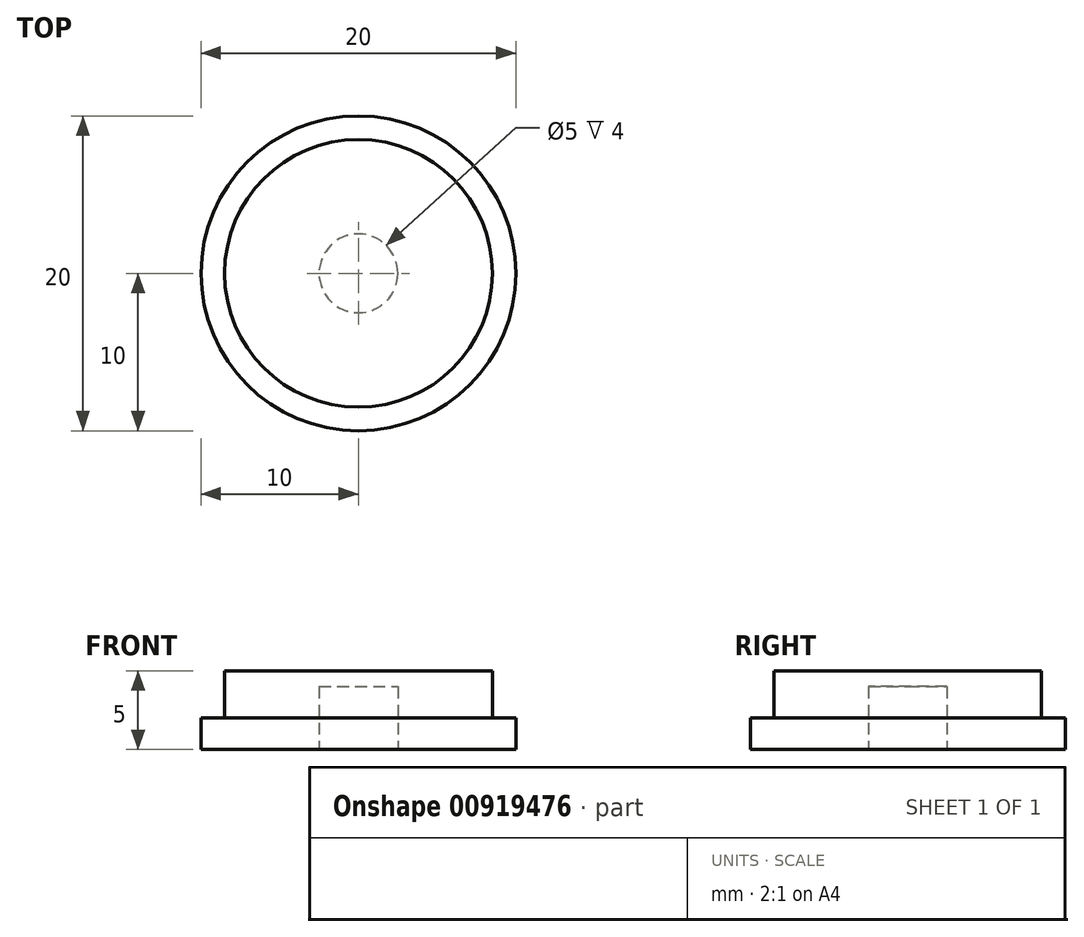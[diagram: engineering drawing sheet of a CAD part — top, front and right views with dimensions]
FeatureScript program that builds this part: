
annotation { "Feature Type Name" : "Feature", "Feature Type Description" : "" }
export const myFeature = defineFeature(function(context is Context, id is Id, definition is map)
    precondition{}
    {
        {
            var Q0;
            Q0=qCreatedBy(makeId("Top.planeOp"),FACE);
            var sketch = newSketch(context, id + "F0", { "sketchPlane" : qUnion([Q0])});
            skCircle(sketch, "E0", {"center": v(0, 0) * mm, "radius": 10 * mm});
            skSolve(sketch);
        }
        {
            var Q0;
            Q0 = qSketchRegion(id + "F0", true);
            extrude(context, id + "F1", {"entities" : qUnion([Q0]), "depth" : 5 * mm, "offsetDistance" : 25 * mm, "symmetric" : true});
        }
        {
            var Q0;
            Q0=makeQuery(id+"F1.opExtrude","CAP_FACE",FACE,{"disambiguationData":[OSD([sQuery(id+"F0.wireOp",EDGE,"E0")])],"isStart":false});
            var sketch = newSketch(context, id + "F2", { "sketchPlane" : qUnion([Q0])});
            skCircle(sketch, "E1", {"center": v(0, 0) * mm, "radius": 10 * mm});
            skCircle(sketch, "E2.0", {"center": v(0, 0) * mm, "radius": 8.5 * mm});
            skSolve(sketch);
        }
        {
            var Q0;
            Q0 = qSketchRegion(id + "F2", true);
            extrude(context, id + "F3", {"entities" : qUnion([Q0]), "operationType" : NewBodyOperationType.REMOVE, "oppositeDirection" : true, "depth" : 3 * mm, "offsetDistance" : 25 * mm});
        }
        {
            var Q0;
            Q0=makeQuery(id+"F1.opExtrude","CAP_FACE",FACE,{"disambiguationData":[OSD([sQuery(id+"F0.wireOp",EDGE,"E0")])],"isStart":true});
            var sketch = newSketch(context, id + "F4", { "sketchPlane" : qUnion([Q0])});
            skCircle(sketch, "E3", {"center": v(0, 0) * mm, "radius": 2.5 * mm});
            skSolve(sketch);
        }
        {
            var Q0;
            Q0 = qSketchRegion(id + "F4", true);
            extrude(context, id + "F5", {"entities" : qUnion([Q0]), "operationType" : NewBodyOperationType.REMOVE, "oppositeDirection" : true, "depth" : 4 * mm, "offsetDistance" : 25 * mm});
        }
    });
